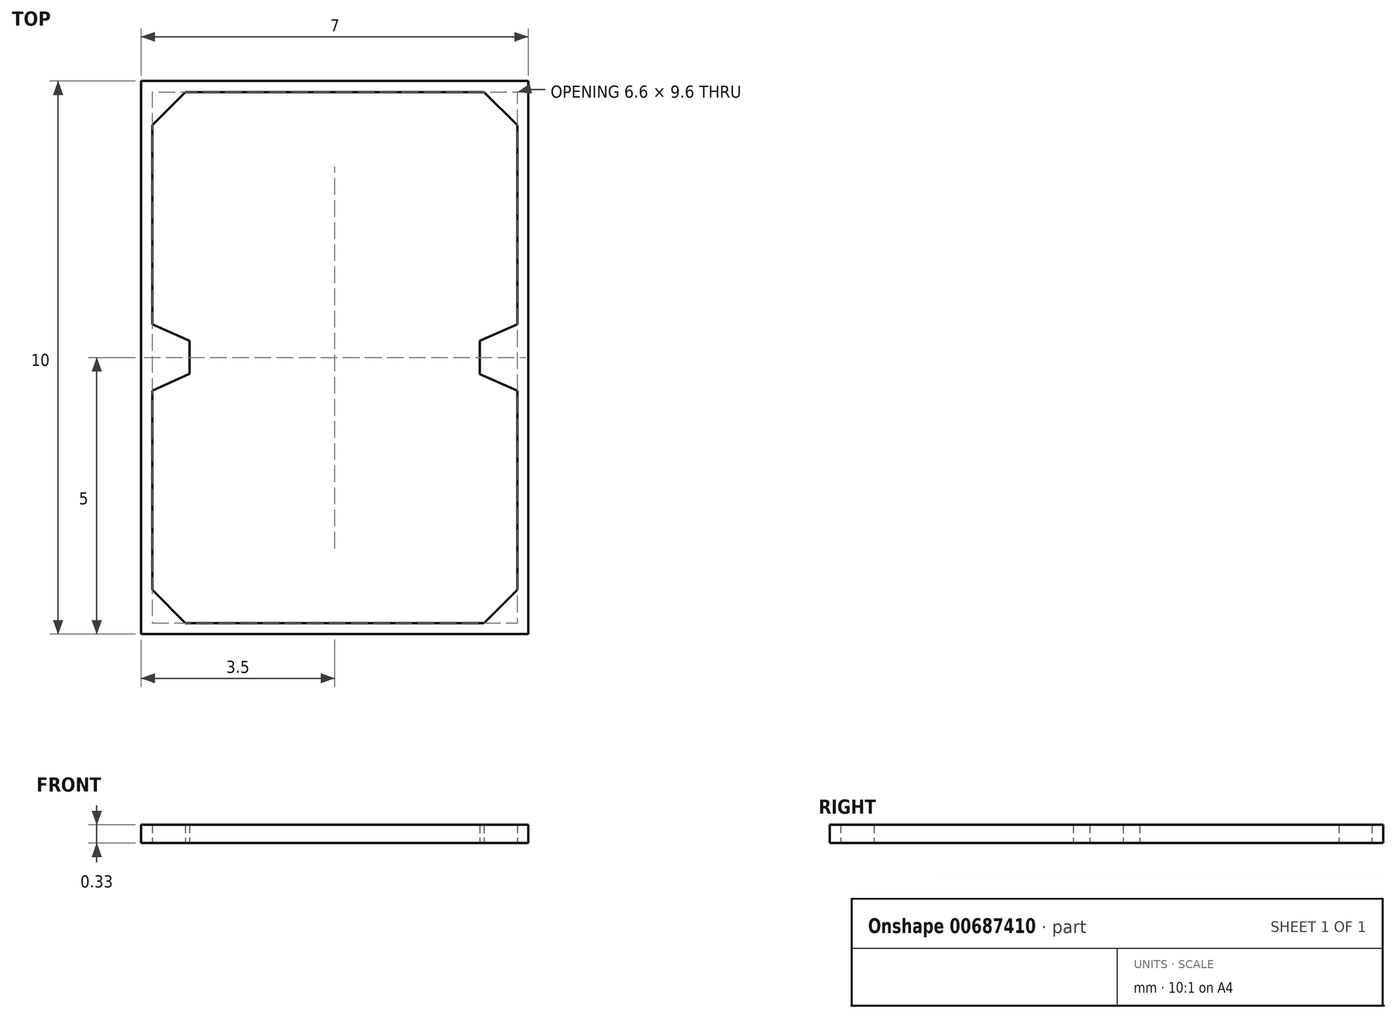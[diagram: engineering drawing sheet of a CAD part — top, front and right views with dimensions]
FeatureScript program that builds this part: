
annotation { "Feature Type Name" : "Feature", "Feature Type Description" : "" }
export const myFeature = defineFeature(function(context is Context, id is Id, definition is map)
    precondition{}
    {
        {
            var Q0;
            Q0=qCreatedBy(makeId("Top.planeOp"),FACE);
            var sketch = newSketch(context, id + "F0", { "sketchPlane" : qUnion([Q0])});
            skLineSegment(sketch, "E0.bottom", {"start": v(7, 23.34) * mm, "end": v(0, 23.34) * mm});
            skLineSegment(sketch, "E0.top", {"start": v(7, 13.34) * mm, "end": v(0, 13.34) * mm});
            skLineSegment(sketch, "E0.left", {"start": v(7, 23.34) * mm, "end": v(7, 13.34) * mm});
            skLineSegment(sketch, "E0.right", {"start": v(0, 23.34) * mm, "end": v(0, 13.34) * mm});
            skLineSegment(sketch, "E1", {"start": v(0, 23.34) * mm, "end": v(1, 23.34) * mm});
            skLineSegment(sketch, "E2", {"start": v(0.8, 23.14) * mm, "end": v(0.2, 22.54) * mm});
            skLineSegment(sketch, "E3", {"start": v(0, 22.34) * mm, "end": v(0, 23.34) * mm});
            skLineSegment(sketch, "E4", {"start": v(7, 23.34) * mm, "end": v(6, 23.34) * mm});
            skLineSegment(sketch, "E5", {"start": v(6.2, 23.14) * mm, "end": v(6.8, 22.54) * mm});
            skLineSegment(sketch, "E6", {"start": v(7, 22.34) * mm, "end": v(7, 23.34) * mm});
            skLineSegment(sketch, "E7", {"start": v(7, 13.34) * mm, "end": v(7, 14.34) * mm});
            skLineSegment(sketch, "E8", {"start": v(6.8, 14.14) * mm, "end": v(6.2, 13.54) * mm});
            skLineSegment(sketch, "E9", {"start": v(6, 13.34) * mm, "end": v(7, 13.34) * mm});
            skLineSegment(sketch, "E10", {"start": v(0, 13.34) * mm, "end": v(0, 14.34) * mm});
            skLineSegment(sketch, "E11", {"start": v(0.2, 14.14) * mm, "end": v(0.8, 13.54) * mm});
            skLineSegment(sketch, "E12", {"start": v(1, 13.34) * mm, "end": v(0, 13.34) * mm});
            skLineSegment(sketch, "E13", {"start": v(0, 13.34) * mm, "end": v(0, 13.54) * mm});
            skLineSegment(sketch, "E14", {"start": v(0.8, 13.54) * mm, "end": v(6.2, 13.54) * mm});
            skPoint(sketch, "E15.endSnap0", {"position": v(6.5, 23.34) * mm});
            skLineSegment(sketch, "E16", {"start": v(6.2, 23.14) * mm, "end": v(0.8, 23.14) * mm});
            skLineSegment(sketch, "E17", {"start": v(0.2, 22.54) * mm, "end": v(0.2, 18.94) * mm});
            skPoint(sketch, "E18.orphan", {"position": v(0, 23.14) * mm});
            skPoint(sketch, "E19.trimOffspring.end.orphan", {"position": v(6.8, 23.34) * mm});
            skPoint(sketch, "E20.trimOffspring.end.orphan", {"position": v(7, 13.54) * mm});
            skPoint(sketch, "E21.orphan", {"position": v(6.8, 13.54) * mm});
            skLineSegment(sketch, "E22", {"start": v(6.8, 22.54) * mm, "end": v(6.8, 18.94) * mm});
            skPoint(sketch, "E23.orphan", {"position": v(0.2, 13.54) * mm});
            skLineSegment(sketch, "E24", {"start": v(0.2, 14.14) * mm, "end": v(0.2, 17.74) * mm});
            skLineSegment(sketch, "E25", {"start": v(0.88, 18.64) * mm, "end": v(0.88, 18.04) * mm});
            skLineSegment(sketch, "E26", {"start": v(0.88, 18.64) * mm, "end": v(0.2, 18.94) * mm});
            skLineSegment(sketch, "E27", {"start": v(0.88, 18.04) * mm, "end": v(0.2, 17.74) * mm});
            skLineSegment(sketch, "E28.trimOffspring", {"start": v(0.2, 17.74) * mm, "end": v(0.2, 14.14) * mm});
            skLineSegment(sketch, "E29", {"start": v(6.12, 18.64) * mm, "end": v(6.12, 18.04) * mm});
            skLineSegment(sketch, "E30", {"start": v(6.12, 18.64) * mm, "end": v(6.8, 18.94) * mm});
            skLineSegment(sketch, "E31", {"start": v(6.12, 18.04) * mm, "end": v(6.8, 17.74) * mm});
            skPoint(sketch, "E32.start.orphan", {"position": v(6.12, 18.94) * mm});
            skPoint(sketch, "E33.start.orphan", {"position": v(6.12, 17.74) * mm});
            skLineSegment(sketch, "E34.trimOffspring", {"start": v(6.8, 17.74) * mm, "end": v(6.8, 14.14) * mm});
            skPoint(sketch, "E35.orphan", {"position": v(0.88, 18.94) * mm});
            skPoint(sketch, "E36.start.orphan", {"position": v(0.88, 17.74) * mm});
            skSolve(sketch);
        }
        {
            var Q0;
            Q0=makeQuery(id+"F0.imprint","IMPRINT",FACE,{"disambiguationData":[TD([[makeQuery(id+"F0.imprint","IMPRINT",EDGE,{"derivedFrom":sQuery(id+"F0.wireOp",EDGE,"E0.bottom")}),1.0]])]});
            extrude(context, id + "F1", {"entities" : qUnion([Q0]), "depth" : 0.33 * mm, "offsetDistance" : 25 * mm});
        }
    });
